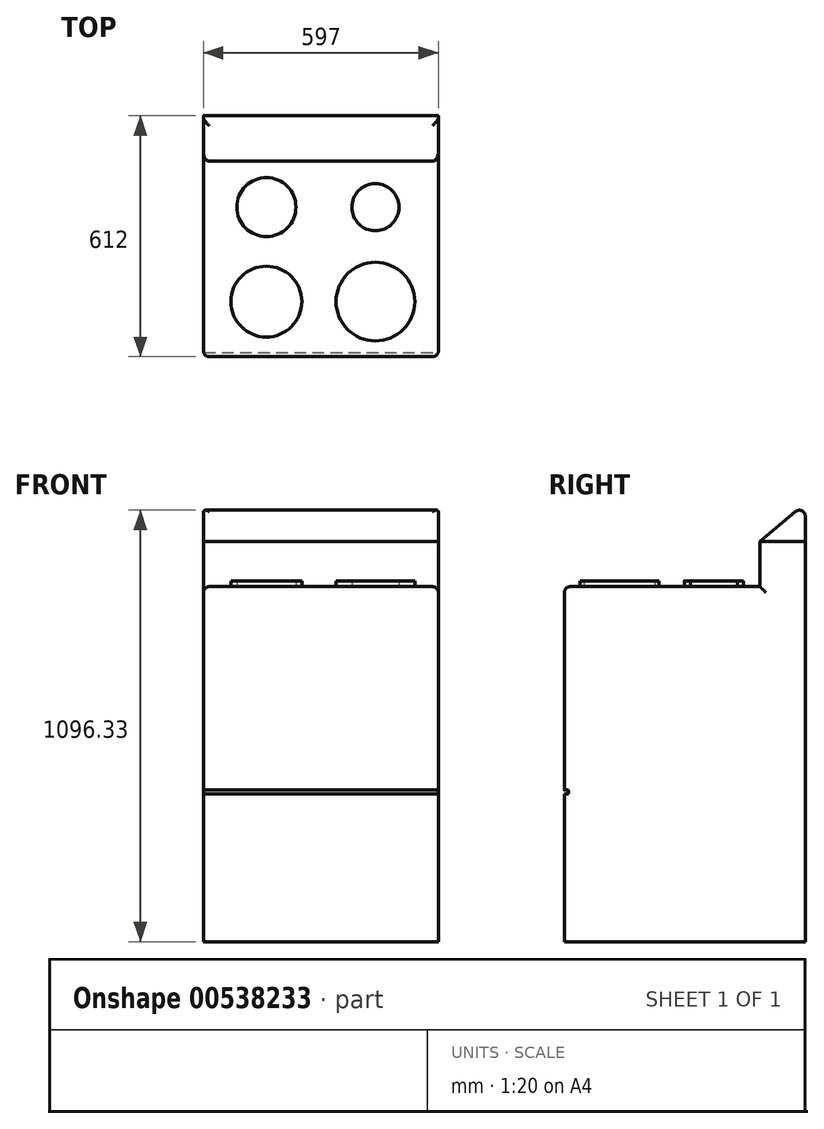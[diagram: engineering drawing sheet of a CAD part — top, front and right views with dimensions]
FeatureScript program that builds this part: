
annotation { "Feature Type Name" : "Feature", "Feature Type Description" : "" }
export const myFeature = defineFeature(function(context is Context, id is Id, definition is map)
    precondition{}
    {
        {
            var Q0;
            Q0=qCreatedBy(makeId("Top.planeOp"),FACE);
            var sketch = newSketch(context, id + "F0", { "sketchPlane" : qUnion([Q0])});
            skLineSegment(sketch, "E0.bottom", {"start": v(0, 0) * mm, "end": v(-597, 0) * mm});
            skLineSegment(sketch, "E0.top", {"start": v(0, 612) * mm, "end": v(-597, 612) * mm});
            skLineSegment(sketch, "E0.left", {"start": v(0, 0) * mm, "end": v(0, 612) * mm});
            skLineSegment(sketch, "E0.right", {"start": v(-597, 0) * mm, "end": v(-597, 612) * mm});
            skSolve(sketch);
        }
        {
            var Q0;
            Q0 = qSketchRegion(id + "F0", true);
            extrude(context, id + "F1", {"entities" : qUnion([Q0]), "depth" : 902 * mm, "offsetDistance" : 25 * mm});
        }
        {
            var Q0;
            Q0=makeQuery(id+"F1.opExtrude","CAP_FACE",FACE,{"disambiguationData":[OSD([sQuery(id+"F0.wireOp",EDGE,"E0.bottom"),sQuery(id+"F0.wireOp",EDGE,"E0.top"),sQuery(id+"F0.wireOp",EDGE,"E0.left"),sQuery(id+"F0.wireOp",EDGE,"E0.right")])],"isStart":false});
            var sketch = newSketch(context, id + "F2", { "sketchPlane" : qUnion([Q0])});
            skLineSegment(sketch, "E1.bottom", {"start": v(-597, 612) * mm, "end": v(0, 612) * mm});
            skLineSegment(sketch, "E1.top", {"start": v(-597, 497) * mm, "end": v(0, 497) * mm});
            skLineSegment(sketch, "E1.left", {"start": v(-597, 612) * mm, "end": v(-597, 497) * mm});
            skLineSegment(sketch, "E1.right", {"start": v(0, 612) * mm, "end": v(0, 497) * mm});
            skSolve(sketch);
        }
        {
            var Q0;
            Q0 = qSketchRegion(id + "F2", true);
            extrude(context, id + "F3", {"entities" : qUnion([Q0]), "operationType" : NewBodyOperationType.ADD, "depth" : 115 * mm, "offsetDistance" : 25 * mm});
        }
        {
            var Q0;
            Q0=qCreatedBy(makeId("Right.planeOp"),FACE);
            var sketch = newSketch(context, id + "F4", { "sketchPlane" : qUnion([Q0])});
            skLineSegment(sketch, "E2.0", {"start": v(497, 1017) * mm, "end": v(612, 1017) * mm});
            skLineSegment(sketch, "E3", {"start": v(497, 1017) * mm, "end": v(612, 1113.5) * mm});
            skLineSegment(sketch, "E4", {"start": v(612, 1113.5) * mm, "end": v(612, 1017) * mm});
            skSolve(sketch);
        }
        {
            var Q0;
            Q0 = qSketchRegion(id + "F4", true);
            extrude(context, id + "F5", {"entities" : qUnion([Q0]), "oppositeDirection" : true, "depth" : 597 * mm, "offsetDistance" : 25 * mm});
        }
        {
            var Q0;
            Q0=makeQuery(id+"F1.opExtrude","CAP_FACE",FACE,{"disambiguationData":[OSD([sQuery(id+"F0.wireOp",EDGE,"E0.bottom"),sQuery(id+"F0.wireOp",EDGE,"E0.top"),sQuery(id+"F0.wireOp",EDGE,"E0.left"),sQuery(id+"F0.wireOp",EDGE,"E0.right")])],"isStart":false});
            var sketch = newSketch(context, id + "F6", { "sketchPlane" : qUnion([Q0])});
            skCircle(sketch, "E5", {"center": v(-437, 140) * mm, "radius": 90 * mm});
            skCircle(sketch, "E6", {"center": v(-437, 380) * mm, "radius": 75 * mm});
            skCircle(sketch, "E7", {"center": v(-160, 380) * mm, "radius": 60 * mm});
            skCircle(sketch, "E8", {"center": v(-160, 140) * mm, "radius": 100 * mm});
            skSolve(sketch);
        }
        {
            var Q0;
            Q0 = qSketchRegion(id + "F6", true);
            extrude(context, id + "F7", {"entities" : qUnion([Q0]), "operationType" : NewBodyOperationType.ADD, "depth" : 15 * mm, "offsetDistance" : 25 * mm});
        }
        {
            var Q0;
            Q0=qCreatedBy(makeId("Right.planeOp"),FACE);
            var sketch = newSketch(context, id + "F8", { "sketchPlane" : qUnion([Q0])});
            skLineSegment(sketch, "E9.bottom", {"start": v(-41.77, 385) * mm, "end": v(10, 385) * mm});
            skLineSegment(sketch, "E9.top", {"start": v(-41.77, 375) * mm, "end": v(10, 375) * mm});
            skLineSegment(sketch, "E9.left", {"start": v(-41.77, 385) * mm, "end": v(-41.77, 375) * mm});
            skLineSegment(sketch, "E9.right", {"start": v(10, 385) * mm, "end": v(10, 375) * mm});
            skSolve(sketch);
        }
        {
            var Q0;
            Q0 = qSketchRegion(id + "F8", true);
            extrude(context, id + "F9", {"entities" : qUnion([Q0]), "operationType" : NewBodyOperationType.REMOVE, "endBound" : BoundingType.THROUGH_ALL, "oppositeDirection" : true, "depth" : 25 * mm, "offsetDistance" : 25 * mm});
        }
        {
            var Q0;
            Q0=makeQuery(id+"F5.opExtrude","SWEPT_EDGE",EDGE,{"disambiguationData":[OSD([sQuery(id+"F4.wireOp",EDGE,"E3"),sQuery(id+"F4.wireOp",EDGE,"E4")])]});
            var Q1;
            Q1=makeQuery(id+"F5.opExtrude","CAP_EDGE",EDGE,{"disambiguationData":[OSD([sQuery(id+"F4.wireOp",EDGE,"E3")])],"isStart":true});
            var Q2;
            Q2=makeQuery(id+"F3.opExtrude","SWEPT_EDGE",EDGE,{"disambiguationData":[OSD([sQuery(id+"F0.wireOp",EDGE,"E0.left"),sQuery(id+"F2.wireOp",EDGE,"E1.top"),sQuery(id+"F2.wireOp",EDGE,"E1.right")])]});
            var Q3;
            Q3=makeQuery(id+"F1.opExtrude","CAP_EDGE",EDGE,{"disambiguationData":[OSD([sQuery(id+"F0.wireOp",EDGE,"E0.left")])],"isStart":false});
            var Q4;
            Q4=makeQuery(id+"F1.opExtrude","CAP_EDGE",EDGE,{"disambiguationData":[OSD([sQuery(id+"F0.wireOp",EDGE,"E0.bottom")])],"isStart":false});
            var Q5;
            {var subQ0=sQuery(id+"F0.wireOp",EDGE,"E0.left");var subQ1=sQuery(id+"F0.wireOp",EDGE,"E0.bottom");Q5=makeQuery(id+"F9.boolean.opBoolean","SPLIT",EDGE,{"disambiguationData":[TD([makeQuery(id+"F9.opExtrude","SWEPT_FACE",FACE,{"disambiguationData":[OSD([sQuery(id+"F8.wireOp",EDGE,"E9.bottom")])]})])],"derivedFrom":makeQuery(id+"F1.opExtrude","SWEPT_EDGE",EDGE,{"disambiguationData":[OSD([subQ1,subQ0])]})});}
            var Q6;
            Q6=makeQuery(id+"F1.opExtrude","CAP_EDGE",EDGE,{"disambiguationData":[OSD([sQuery(id+"F0.wireOp",EDGE,"E0.right")])],"isStart":false});
            var Q7;
            Q7=makeQuery(id+"F3.opExtrude","SWEPT_EDGE",EDGE,{"disambiguationData":[OSD([sQuery(id+"F0.wireOp",EDGE,"E0.right"),sQuery(id+"F2.wireOp",EDGE,"E1.top"),sQuery(id+"F2.wireOp",EDGE,"E1.left")])]});
            var Q8;
            Q8=makeQuery(id+"F5.opExtrude","CAP_EDGE",EDGE,{"disambiguationData":[OSD([sQuery(id+"F4.wireOp",EDGE,"E3")])],"isStart":false});
            var Q9;
            {var subQ0=sQuery(id+"F0.wireOp",EDGE,"E0.right");var subQ1=sQuery(id+"F0.wireOp",EDGE,"E0.bottom");Q9=makeQuery(id+"F9.boolean.opBoolean","SPLIT",EDGE,{"disambiguationData":[TD([makeQuery(id+"F9.opExtrude","SWEPT_FACE",FACE,{"disambiguationData":[OSD([sQuery(id+"F8.wireOp",EDGE,"E9.bottom")])]})])],"derivedFrom":makeQuery(id+"F1.opExtrude","SWEPT_EDGE",EDGE,{"disambiguationData":[OSD([subQ1,subQ0])]})});}
            fillet(context, id + "F10", {"entities" : qUnion([Q0, Q1, Q2, Q3, Q4, Q5, Q6, Q7, Q8, Q9]), "radius" : 15 * mm, "tangentPropagation" : true, "allowEdgeOverflow" : false});
        }
    });
